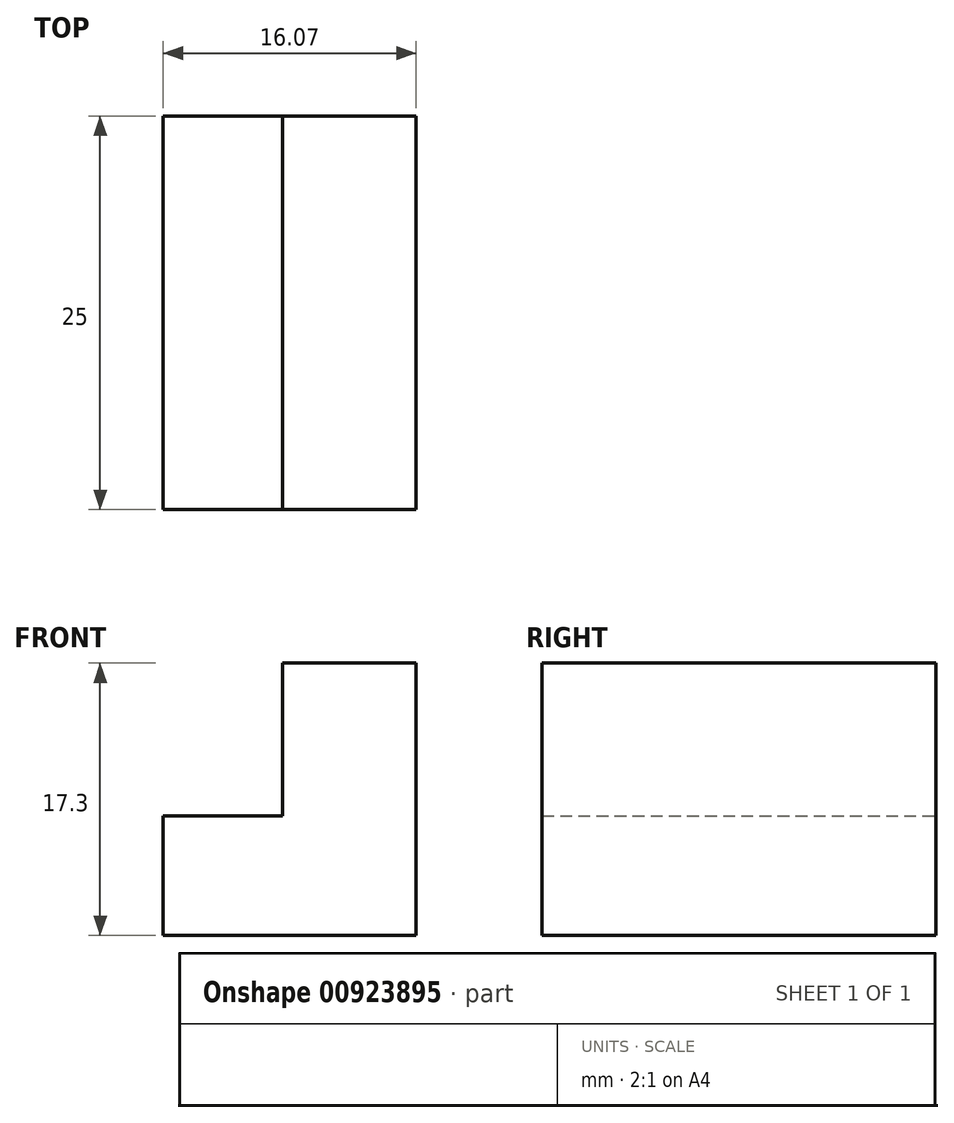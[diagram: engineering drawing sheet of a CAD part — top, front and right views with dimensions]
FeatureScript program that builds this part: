
annotation { "Feature Type Name" : "Feature", "Feature Type Description" : "" }
export const myFeature = defineFeature(function(context is Context, id is Id, definition is map)
    precondition{}
    {
        {
            var Q0;
            Q0=qCreatedBy(makeId("Front.planeOp"),FACE);
            var sketch = newSketch(context, id + "F0", { "sketchPlane" : qUnion([Q0])});
            skLineSegment(sketch, "E0", {"start": v(23.2, 0) * mm, "end": v(23.2, 7.6) * mm});
            skLineSegment(sketch, "E1", {"start": v(23.2, 7.6) * mm, "end": v(30.78, 7.6) * mm});
            skLineSegment(sketch, "E2", {"start": v(30.78, 7.6) * mm, "end": v(30.78, 17.3) * mm});
            skLineSegment(sketch, "E3", {"start": v(30.78, 17.3) * mm, "end": v(39.28, 17.3) * mm});
            skLineSegment(sketch, "E4", {"start": v(39.28, 17.3) * mm, "end": v(39.28, 0) * mm});
            skLineSegment(sketch, "E5", {"start": v(39.28, 0) * mm, "end": v(23.2, 0) * mm});
            skSolve(sketch);
        }
        {
            var Q0;
            Q0 = qSketchRegion(id + "F0", true);
            extrude(context, id + "F1", {"entities" : qUnion([Q0]), "depth" : 25 * mm, "offsetDistance" : 25 * mm});
        }
    });
